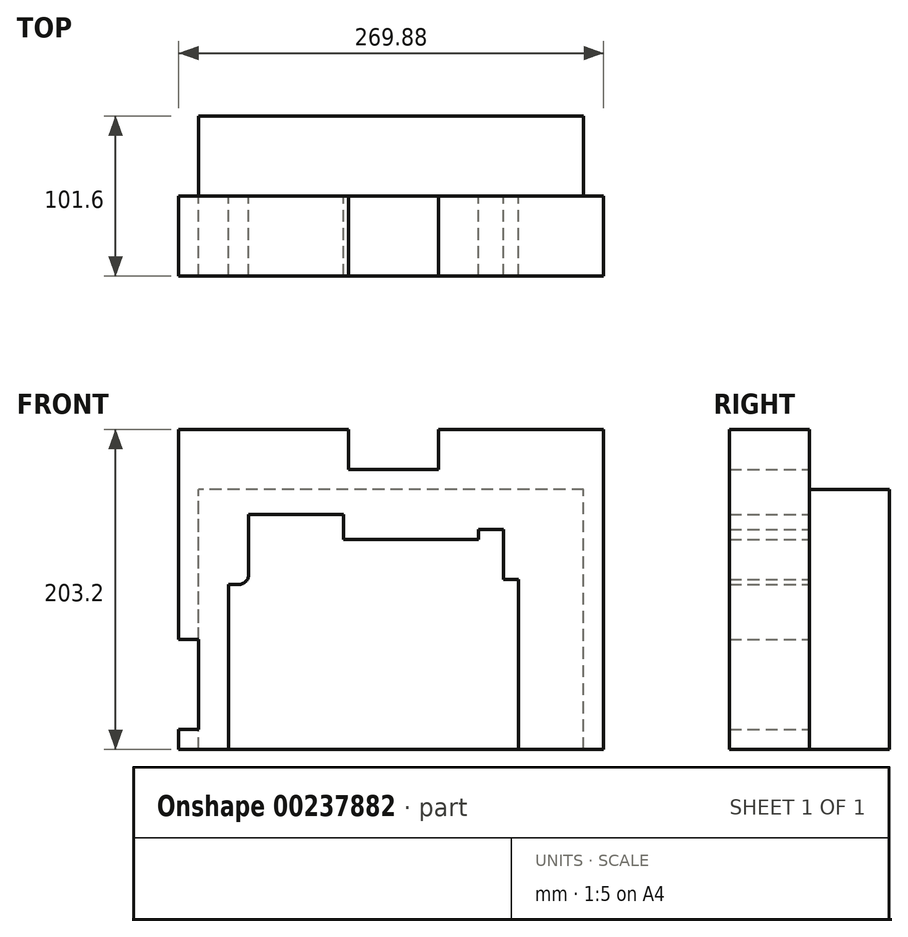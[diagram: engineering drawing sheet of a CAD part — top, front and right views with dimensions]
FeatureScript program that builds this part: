
annotation { "Feature Type Name" : "Feature", "Feature Type Description" : "" }
export const myFeature = defineFeature(function(context is Context, id is Id, definition is map)
    precondition{}
    {
        {
            var Q0;
            Q0=qCreatedBy(makeId("Front.planeOp"),FACE);
            var sketch = newSketch(context, id + "F0", { "sketchPlane" : qUnion([Q0])});
            skLineSegment(sketch, "E0.bottom", {"start": v(0, 0) * mm, "end": v(269.88, 0) * mm, "construction": true});
            skLineSegment(sketch, "E0.top", {"start": v(0, 203.2) * mm, "end": v(269.88, 203.2) * mm, "construction": true});
            skLineSegment(sketch, "E0.left", {"start": v(0, 0) * mm, "end": v(0, 203.2) * mm, "construction": true});
            skLineSegment(sketch, "E0.right", {"start": v(269.88, 0) * mm, "end": v(269.88, 203.2) * mm, "construction": true});
            skLineSegment(sketch, "E1", {"start": v(0, 0) * mm, "end": v(0, 12.7) * mm});
            skLineSegment(sketch, "E2", {"start": v(0, 12.7) * mm, "end": v(12.7, 12.7) * mm});
            skLineSegment(sketch, "E3", {"start": v(12.7, 12.7) * mm, "end": v(12.7, 69.85) * mm});
            skLineSegment(sketch, "E4", {"start": v(12.7, 69.85) * mm, "end": v(0, 69.85) * mm});
            skLineSegment(sketch, "E5", {"start": v(0, 69.85) * mm, "end": v(0, 203.2) * mm});
            skLineSegment(sketch, "E6", {"start": v(0, 203.2) * mm, "end": v(107.95, 203.2) * mm});
            skLineSegment(sketch, "E7", {"start": v(107.95, 203.2) * mm, "end": v(107.95, 177.8) * mm});
            skLineSegment(sketch, "E8", {"start": v(107.95, 177.8) * mm, "end": v(165.1, 177.8) * mm});
            skLineSegment(sketch, "E9", {"start": v(165.1, 177.8) * mm, "end": v(165.1, 203.2) * mm});
            skLineSegment(sketch, "E10", {"start": v(165.1, 203.2) * mm, "end": v(269.88, 203.2) * mm});
            skLineSegment(sketch, "E11", {"start": v(269.88, 203.2) * mm, "end": v(269.88, 0) * mm});
            skLineSegment(sketch, "E12", {"start": v(215.9, 0) * mm, "end": v(215.9, 107.95) * mm});
            skLineSegment(sketch, "E13", {"start": v(215.9, 107.95) * mm, "end": v(206.38, 107.95) * mm});
            skLineSegment(sketch, "E14", {"start": v(206.38, 107.95) * mm, "end": v(206.38, 139.7) * mm});
            skLineSegment(sketch, "E15", {"start": v(206.38, 139.7) * mm, "end": v(190.5, 139.7) * mm});
            skLineSegment(sketch, "E16", {"start": v(190.5, 139.7) * mm, "end": v(190.5, 133.35) * mm});
            skLineSegment(sketch, "E17", {"start": v(190.5, 133.35) * mm, "end": v(104.78, 133.35) * mm});
            skLineSegment(sketch, "E18", {"start": v(104.78, 133.35) * mm, "end": v(104.78, 149.22) * mm});
            skLineSegment(sketch, "E19", {"start": v(104.78, 149.22) * mm, "end": v(44.45, 149.22) * mm});
            skLineSegment(sketch, "E20", {"start": v(44.45, 149.22) * mm, "end": v(44.45, 111.12) * mm});
            skLineSegment(sketch, "E21", {"start": v(0, 0) * mm, "end": v(31.75, 0) * mm});
            skLineSegment(sketch, "E22", {"start": v(31.75, 0) * mm, "end": v(31.75, 104.78) * mm});
            skLineSegment(sketch, "E23", {"start": v(31.75, 104.78) * mm, "end": v(38.1, 104.78) * mm});
            skArc(sketch, "E24", {"start": v(38.1, 104.78) * mm, "mid": v(42.6, 106.63) * mm, "end": v(44.45, 111.12) * mm});
            skLineSegment(sketch, "E25", {"start": v(269.88, 0) * mm, "end": v(215.9, 0) * mm});
            skSolve(sketch);
        }
        {
            var Q0;
            Q0 = qSketchRegion(id + "F0", true);
            extrude(context, id + "F1", {"entities" : qUnion([Q0]), "depth" : 50.8 * mm});
        }
        {
            var Q0;
            Q0=makeQuery(id+"F1.opExtrude","CAP_FACE",FACE,{"disambiguationData":[OSD([sQuery(id+"F0.wireOp",EDGE,"E1"),sQuery(id+"F0.wireOp",EDGE,"E2"),sQuery(id+"F0.wireOp",EDGE,"E3"),sQuery(id+"F0.wireOp",EDGE,"E4"),sQuery(id+"F0.wireOp",EDGE,"E5"),sQuery(id+"F0.wireOp",EDGE,"E6"),sQuery(id+"F0.wireOp",EDGE,"E7"),sQuery(id+"F0.wireOp",EDGE,"E8"),sQuery(id+"F0.wireOp",EDGE,"E9"),sQuery(id+"F0.wireOp",EDGE,"E10"),sQuery(id+"F0.wireOp",EDGE,"E11"),sQuery(id+"F0.wireOp",EDGE,"E12"),sQuery(id+"F0.wireOp",EDGE,"E13"),sQuery(id+"F0.wireOp",EDGE,"E14"),sQuery(id+"F0.wireOp",EDGE,"E15"),sQuery(id+"F0.wireOp",EDGE,"E16"),sQuery(id+"F0.wireOp",EDGE,"E17"),sQuery(id+"F0.wireOp",EDGE,"E18"),sQuery(id+"F0.wireOp",EDGE,"E19"),sQuery(id+"F0.wireOp",EDGE,"E20"),sQuery(id+"F0.wireOp",EDGE,"E21"),sQuery(id+"F0.wireOp",EDGE,"E22"),sQuery(id+"F0.wireOp",EDGE,"E23"),sQuery(id+"F0.wireOp",EDGE,"E24"),sQuery(id+"F0.wireOp",EDGE,"E25")])],"isStart":true});
            var sketch = newSketch(context, id + "F2", { "sketchPlane" : qUnion([Q0])});
            skLineSegment(sketch, "E26.bottom", {"start": v(-257.18, 0) * mm, "end": v(-12.7, 0) * mm});
            skLineSegment(sketch, "E26.top", {"start": v(-257.18, 165.1) * mm, "end": v(-12.7, 165.1) * mm});
            skLineSegment(sketch, "E26.left", {"start": v(-257.18, 0) * mm, "end": v(-257.18, 165.1) * mm});
            skLineSegment(sketch, "E26.right", {"start": v(-12.7, 0) * mm, "end": v(-12.7, 165.1) * mm});
            skSolve(sketch);
        }
        {
            var Q0;
            Q0 = qSketchRegion(id + "F2", true);
            extrude(context, id + "F3", {"entities" : qUnion([Q0]), "depth" : 50.8 * mm});
        }
    });
